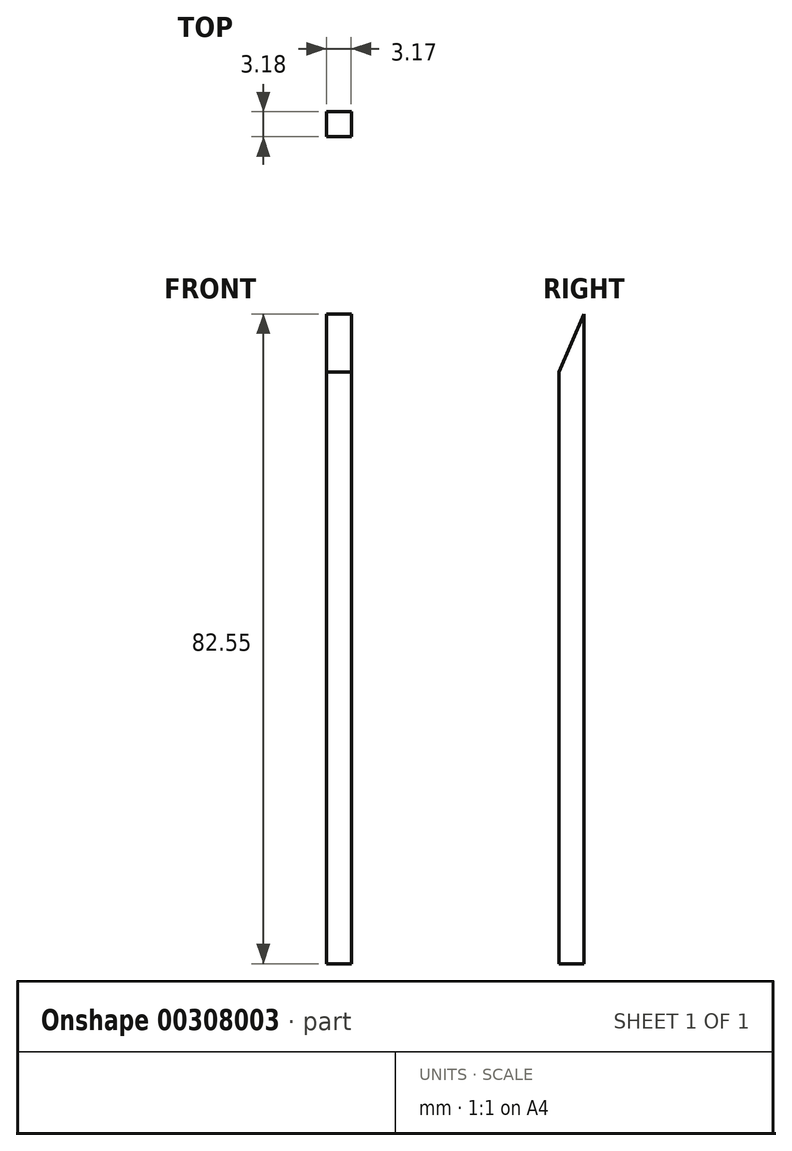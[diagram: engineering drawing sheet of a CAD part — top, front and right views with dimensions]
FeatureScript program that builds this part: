
annotation { "Feature Type Name" : "Feature", "Feature Type Description" : "" }
export const myFeature = defineFeature(function(context is Context, id is Id, definition is map)
    precondition{}
    {
        {
            var Q0;
            Q0=qCreatedBy(makeId("Right.planeOp"),FACE);
            var sketch = newSketch(context, id + "F0", { "sketchPlane" : qUnion([Q0])});
            skLineSegment(sketch, "E0", {"start": v(3.18, 82.55) * mm, "end": v(3.18, 0) * mm});
            skLineSegment(sketch, "E1", {"start": v(0, 75.14) * mm, "end": v(0, 0) * mm});
            skLineSegment(sketch, "E2", {"start": v(3.18, 82.55) * mm, "end": v(0, 75.14) * mm});
            skLineSegment(sketch, "E3", {"start": v(3.18, 0) * mm, "end": v(0, 0) * mm});
            skSolve(sketch);
        }
        {
            var Q0;
            Q0=makeQuery(id+"F0.imprint","IMPRINT",FACE,{"disambiguationData":[TD([[makeQuery(id+"F0.imprint","IMPRINT",EDGE,{"derivedFrom":sQuery(id+"F0.wireOp",EDGE,"c0QTC3x4-7hKF-fHSz-BBoa-AbxE8aln1B4O")}),-1.0]])]});
            var Q1;
            {var subQ0=sQuery(id+"F0.wireOp",EDGE,"E0");Q1=makeQuery(id+"F0.imprint","IMPRINT",FACE,{"disambiguationData":[TD([[makeQuery(id+"F0.imprint","IMPRINT",EDGE,{"derivedFrom":subQ0}),-1.0]])]});}
            var Q2;
            {var subQ0=sQuery(id+"F0.wireOp",EDGE,"Zd5pBiKY-3EBp-Sm5Y-wHDk-2GRI8JiMUKWk");Q2=makeQuery(id+"F0.imprint","IMPRINT",FACE,{"disambiguationData":[TD([[makeQuery(id+"F0.imprint","IMPRINT",EDGE,{"derivedFrom":subQ0}),1.0]])]});}
            extrude(context, id + "F1", {"entities" : qUnion([Q0, Q1, Q2]), "depth" : 3.17 * mm});
        }
    });
